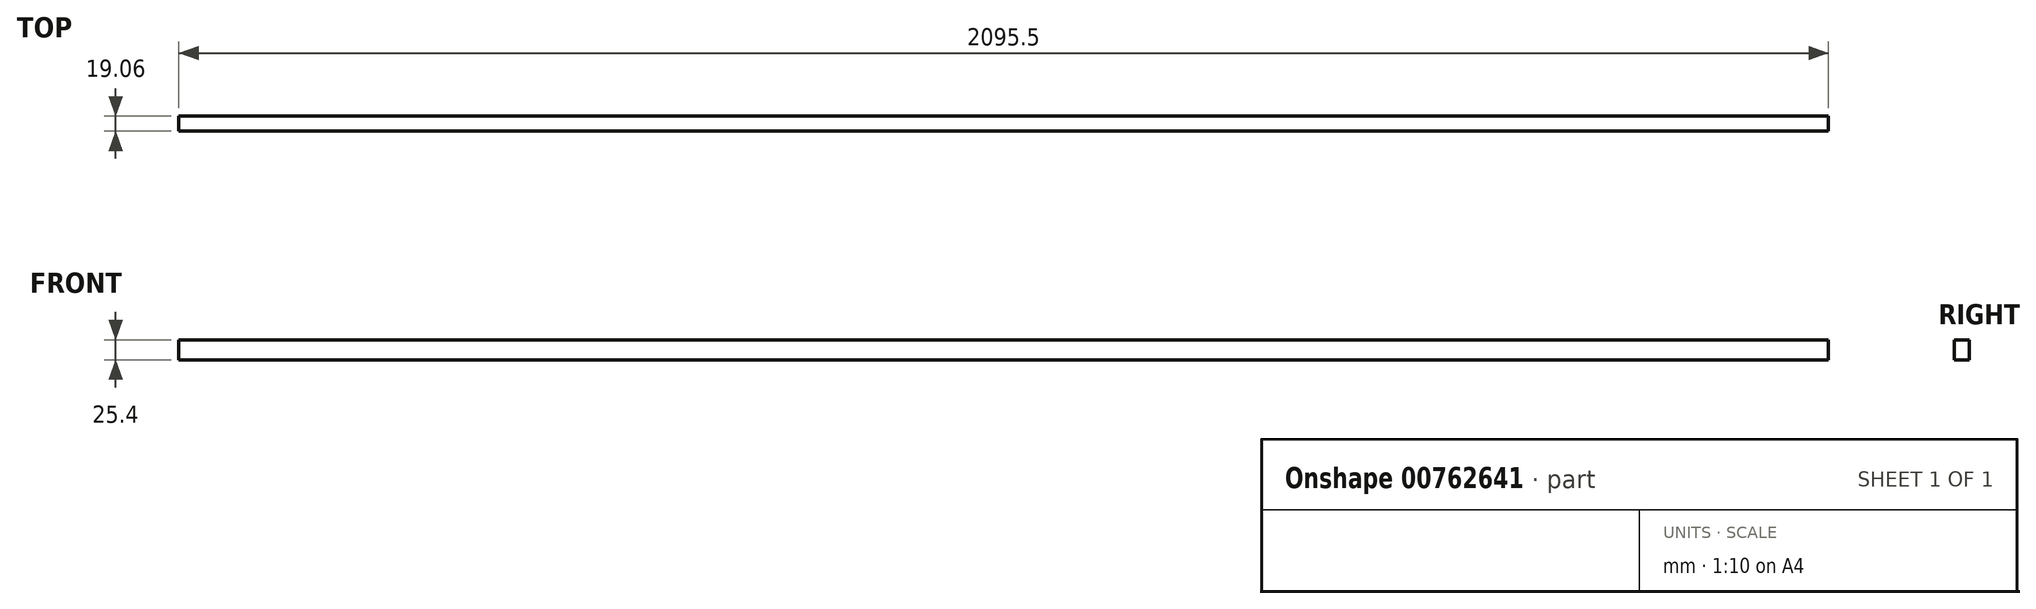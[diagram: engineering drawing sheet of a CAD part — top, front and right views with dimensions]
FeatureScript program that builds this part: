
annotation { "Feature Type Name" : "Feature", "Feature Type Description" : "" }
export const myFeature = defineFeature(function(context is Context, id is Id, definition is map)
    precondition{}
    {
        {
            var Q0;
            Q0=qCreatedBy(makeId("Top.planeOp"),FACE);
            var sketch = newSketch(context, id + "F0", { "sketchPlane" : qUnion([Q0])});
            skLineSegment(sketch, "E0.bottom", {"start": v(-1047.75, 9.53) * mm, "end": v(1047.75, 9.53) * mm});
            skLineSegment(sketch, "E0.top", {"start": v(-1047.75, -9.53) * mm, "end": v(1047.75, -9.53) * mm});
            skLineSegment(sketch, "E0.left", {"start": v(-1047.75, 9.53) * mm, "end": v(-1047.75, -9.53) * mm});
            skLineSegment(sketch, "E0.right", {"start": v(1047.75, 9.53) * mm, "end": v(1047.75, -9.53) * mm});
            skPoint(sketch, "E0.middle", {"position": v(0, 0) * mm});
            skSolve(sketch);
        }
        {
            var Q0;
            Q0=makeQuery(id+"F0.imprint","IMPRINT",FACE,{"disambiguationData":[TD([[makeQuery(id+"F0.imprint","IMPRINT",EDGE,{"derivedFrom":sQuery(id+"F0.wireOp",EDGE,"E0.bottom")}),-1.0]])]});
            extrude(context, id + "F1", {"entities" : qUnion([Q0]), "depth" : 25.4 * mm, "offsetDistance" : 25.4 * mm});
        }
    });
